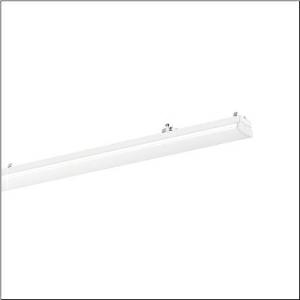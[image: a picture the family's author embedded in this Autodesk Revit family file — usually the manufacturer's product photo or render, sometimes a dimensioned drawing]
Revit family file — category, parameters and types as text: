
# Revit family: licross_21_recessed_opal_mo_52tl1ddn425g
name_source: partatom
category: Lighting Fixtures
units: mm (PartAtom-declared; Revit-internal decimal feet)

## family parameters
Cut with Voids When Loaded = No
Host = Face
Light Source = No
Part Type = Normal
Room Calculation Point = No
Round Connector Dimension = Use Diameter
Shared = No

## types (1)
- --- (1 x LED, 2750 lm, 16.2 W, 4000K)
    Apparent Load = 16 VA
    CIE Flux Codes = 44 73 91 87 100
    Color Rendering = 80
    Color Temperature = 4000K
    Default Elevation = 1800 mm
    Description = Licross 21 recessed opal MO, luminaire insert, of sheet steel, galvanised, coil coated, white, length: 1.500mm, width: 66mm, height: 67mm, LED rated luminous flux: 2.750lm, light colour: 840, SDCM (Standard Deviation of Colour Matching)MacAdam ≤ 3 SDCM (initial), control gear: DALI 2, with plug, 5-pole, with phase selection, mains connection: 220..240V, AC, 50/60Hz, rated input power: 16W, internal wiring halogen-free, primary optical cover: cover, of PMMA, light emission: direct with ceiling illumination distribution, primary light characteristic: symmetric, protection rating (complete): IP40, insulation class (complete): insulation class I (protective earthing), certification: CE, ENEC, VDE, UKCA, protection symbol: D if used in an environment without relevant dust loads with corresponding accessories, impact resistance: IK06, permissible ambient temperature for indoor applications: -25..+50°C, corresponds to IFS (International Featured Standards) requirements for safety and quality in the food industry, reducing of maximum allowable ambient temperature of 5°C with ceiling mounting, LABS conformity tested according to VDMA 24364:2018-05, The light source and the operating device comply with the requirements of the Ecodesign Regulation (EU) 2019/2020 and are replaceable in accordance with this regulation, packaging unit: 1 piece
    Height = 83 mm
    Lamp = 1 x LED
    Lamp Light Flux = 2750 lm
    Lamp Power = 16.2 W
    Lamp count = 1
    Length = 1500 mm
    Luminous efficacy = 170 lm/W
    Manufacturer = Siteco
    ModVariant = No
    Model = 52TL1DDN425G
    Mounting Place = Ceiling
    Mounting Type = Pendant
    Number of Poles = 1
    OnlyDefault = Yes
    Power Factor = 1
    Product Name = Licross 21 recessed opal MO
    Product group = luminaire insert | ceiling pendant
    ProductGroupID = 901
    Protection Class = Protection class I
    Protection Degree = IP 40
    RLX_Detail_Level = 1
    RLX_Emergency_Light_Flux = 0 lm
    RLX_Emergency_Type = 0
    RLX_Emergency_Type_DB = No
    RlxData = <blob elided: 26217 chars, md5=15171070>
    Socket = socket
    Standby Power = 0 W
    System Light Flux = 2750 lm
    System Power = 16 W
    Type Comments = factory setting: luminous flux: 100 % | dim-lin: 254 | 104 mA
    Type Image = l_1313666.jpg
    URL = http://relux.com
    VarID = @adj_070839
    Voltage = 0 V
    Weight = 0.00 kg
    Width = 76 mm

## geometry (parser evidence)
native form markers: Blend x4, Sweep x13
no freeform markers — native parametric forms only
